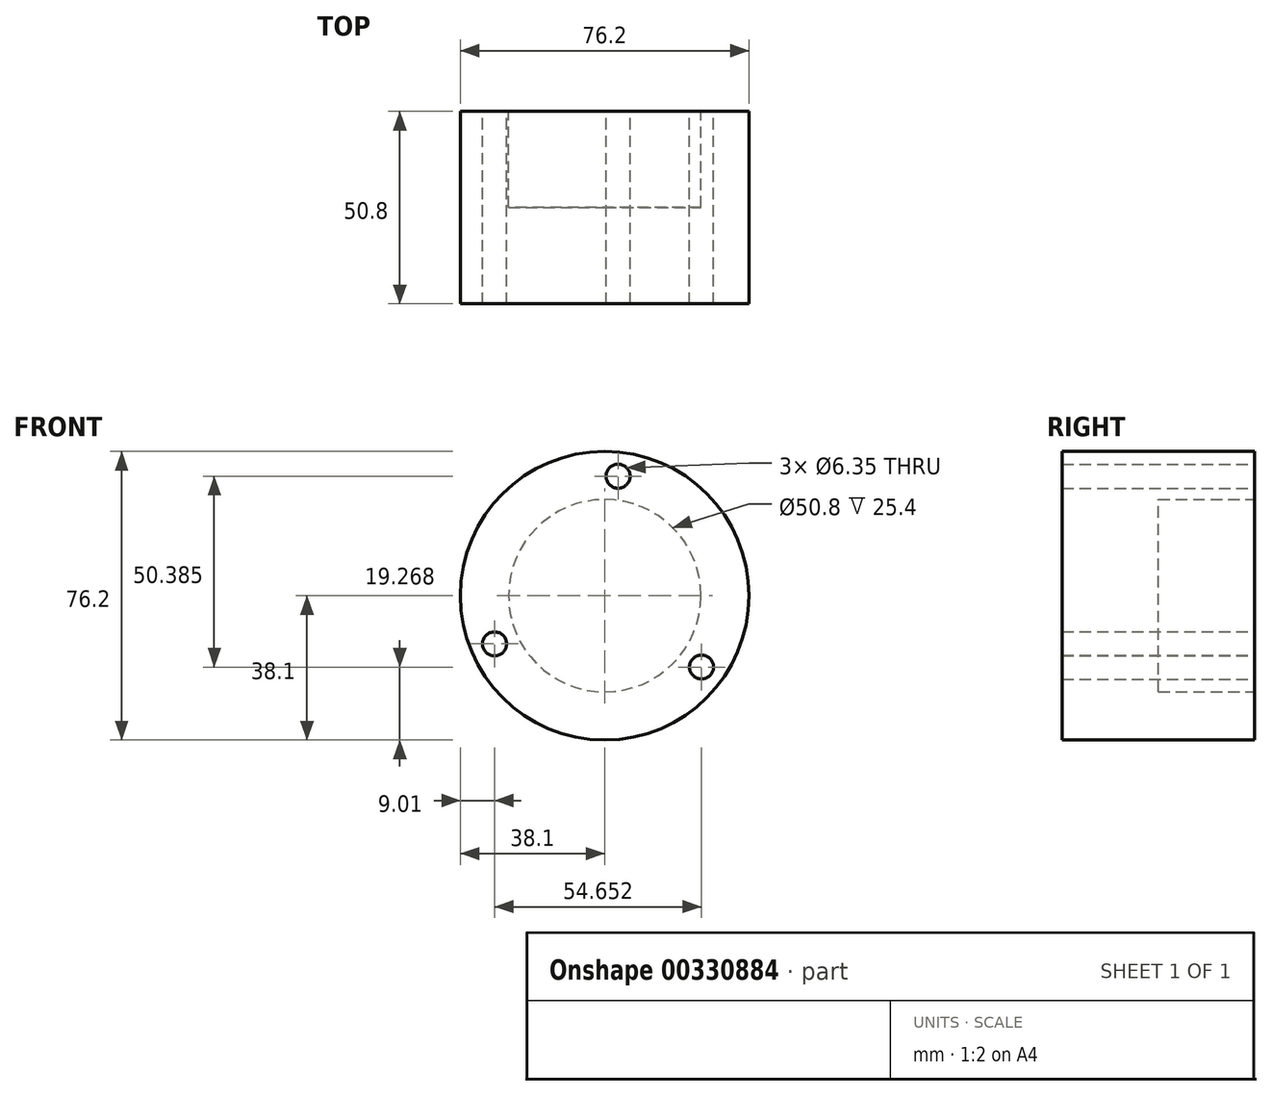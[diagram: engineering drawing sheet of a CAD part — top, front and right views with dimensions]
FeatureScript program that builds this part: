
annotation { "Feature Type Name" : "Feature", "Feature Type Description" : "" }
export const myFeature = defineFeature(function(context is Context, id is Id, definition is map)
    precondition{}
    {
        {
            var Q0;
            Q0=qCreatedBy(makeId("Front.planeOp"),FACE);
            var sketch = newSketch(context, id + "F0", { "sketchPlane" : qUnion([Q0])});
            skCircle(sketch, "E0", {"center": v(0, 0) * mm, "radius": 38.1 * mm});
            skCircle(sketch, "E1", {"center": v(3.53, 31.55) * mm, "radius": 3.18 * mm});
            skCircle(sketch, "E2.1.0", {"center": v(-29.09, -12.72) * mm, "radius": 3.18 * mm});
            skCircle(sketch, "E2.2.0", {"center": v(25.56, -18.83) * mm, "radius": 3.18 * mm});
            skCircle(sketch, "E3.0", {"center": v(0, 0) * mm, "radius": 25.4 * mm});
            skSolve(sketch);
        }
        {
            var Q0;
            Q0=makeQuery(id+"F0.imprint","IMPRINT",FACE,{"disambiguationData":[TD([[makeQuery(id+"F0.imprint","IMPRINT",EDGE,{"derivedFrom":sQuery(id+"F0.wireOp",EDGE,"E0")}),1.0]])]});
            extrude(context, id + "F1", {"entities" : qUnion([Q0]), "endBound" : BoundingType.SYMMETRIC, "depth" : 50.8 * mm});
        }
        {
            var Q0;
            Q0=makeQuery(id+"F0.imprint","IMPRINT",FACE,{"disambiguationData":[TD([[makeQuery(id+"F0.imprint","IMPRINT",EDGE,{"derivedFrom":sQuery(id+"F0.wireOp",EDGE,"E3.0")}),1.0]])]});
            var Q1;
            Q1=makeQuery(id+"F1.opExtrude","CAP_FACE",FACE,{"disambiguationData":[OSD([sQuery(id+"F0.wireOp",EDGE,"E0"),sQuery(id+"F0.wireOp",EDGE,"E1"),sQuery(id+"F0.wireOp",EDGE,"E2.1.0"),sQuery(id+"F0.wireOp",EDGE,"E2.2.0"),sQuery(id+"F0.wireOp",EDGE,"E3.0")])],"isStart":false});
            extrude(context, id + "F2", {"entities" : qUnion([Q0]), "operationType" : NewBodyOperationType.ADD, "endBound" : BoundingType.UP_TO_SURFACE, "endBoundEntityFace" : qUnion([Q1]), "depth" : 48.26 * mm});
        }
    });
